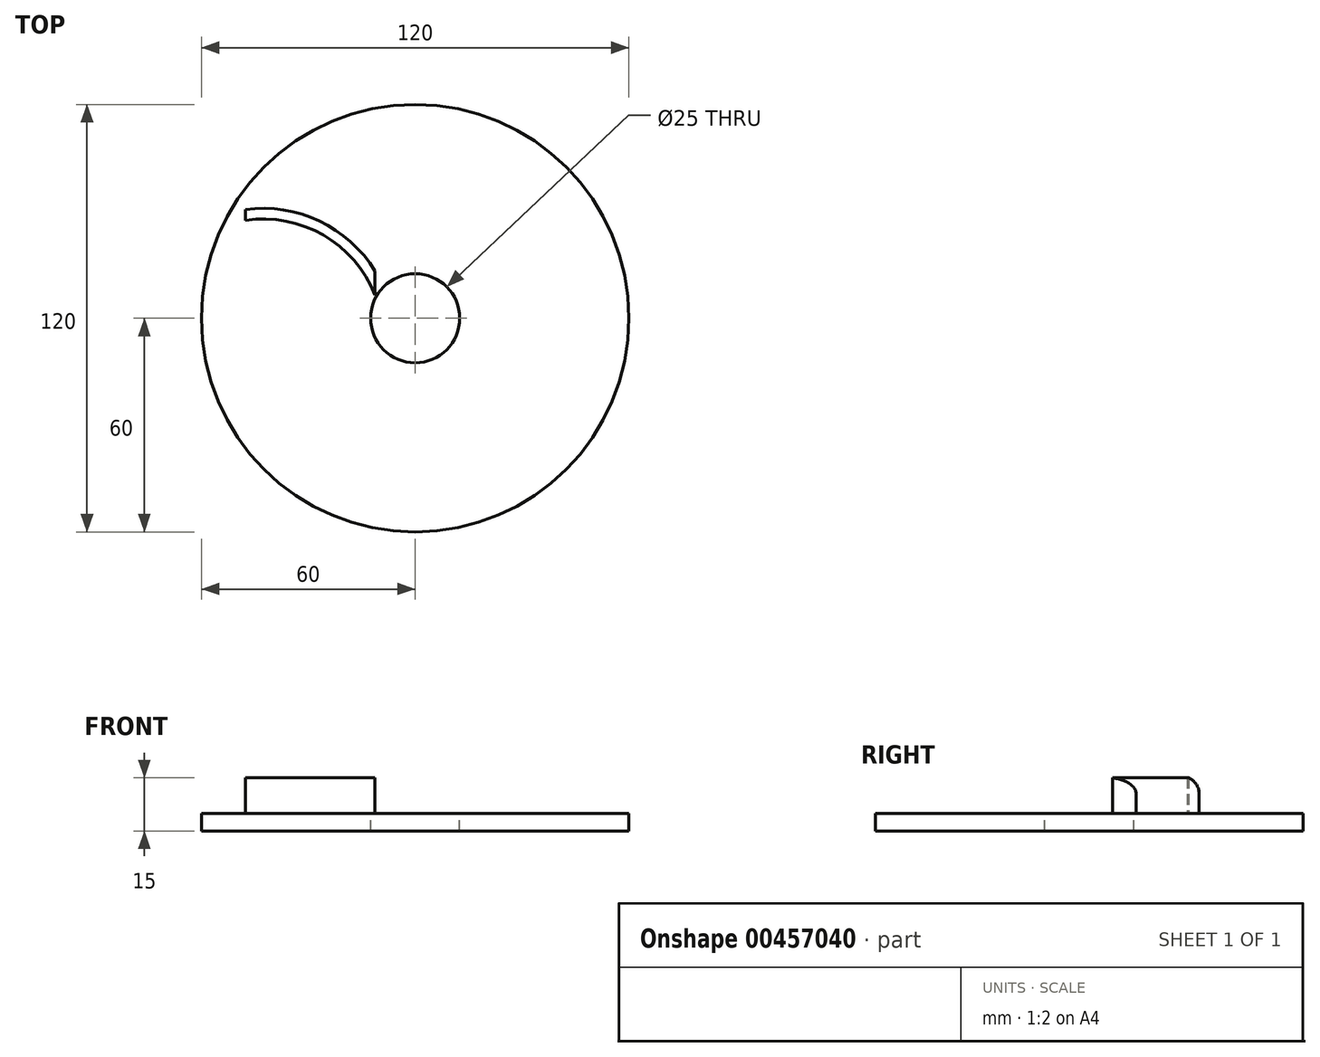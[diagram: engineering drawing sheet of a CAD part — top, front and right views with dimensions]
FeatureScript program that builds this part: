
annotation { "Feature Type Name" : "Feature", "Feature Type Description" : "" }
export const myFeature = defineFeature(function(context is Context, id is Id, definition is map)
    precondition{}
    {
        {
            var Q0;
            Q0=qCreatedBy(makeId("Top.planeOp"),FACE);
            var sketch = newSketch(context, id + "F0", { "sketchPlane" : qUnion([Q0])});
            skCircle(sketch, "E0", {"center": v(0, 0) * mm, "radius": 60 * mm});
            skSolve(sketch);
        }
        {
            var Q0;
            Q0 = qSketchRegion(id + "F0", true);
            extrude(context, id + "F1", {"entities" : qUnion([Q0]), "depth" : 5 * mm});
        }
        {
            var Q0;
            Q0=makeQuery(id+"F1.opExtrude","CAP_FACE",FACE,{"disambiguationData":[OSD([sQuery(id+"F0.wireOp",EDGE,"E0")])],"isStart":false});
            var sketch = newSketch(context, id + "F2", { "sketchPlane" : qUnion([Q0])});
            skCircle(sketch, "E1", {"center": v(0, 0) * mm, "radius": 12.5 * mm});
            skSolve(sketch);
        }
        {
            var Q0;
            Q0=makeQuery(id+"F2.imprint","IMPRINT",FACE,{"disambiguationData":[TD([[makeQuery(id+"F2.imprint","IMPRINT",EDGE,{"derivedFrom":sQuery(id+"F2.wireOp",EDGE,"E1")}),1.0]])]});
            extrude(context, id + "F3", {"entities" : qUnion([Q0]), "operationType" : NewBodyOperationType.REMOVE, "oppositeDirection" : true, "depth" : 10 * mm});
        }
        {
            var Q0;
            Q0=makeQuery(id+"F1.opExtrude","CAP_FACE",FACE,{"disambiguationData":[OSD([sQuery(id+"F0.wireOp",EDGE,"E0")])],"isStart":false});
            var sketch = newSketch(context, id + "F4", { "sketchPlane" : qUnion([Q0])});
            skArc(sketch, "E2", {"start": v(-11.26, 6.5) * mm, "mid": v(-25.79, 23.34) * mm, "end": v(-47.63, 27.5) * mm});
            skArc(sketch, "E3.0", {"start": v(-11.26, 13.2) * mm, "mid": v(-26.86, 27.3) * mm, "end": v(-47.63, 30.53) * mm});
            skLineSegment(sketch, "E4", {"start": v(-47.63, 27.5) * mm, "end": v(-47.63, 30.53) * mm});
            skLineSegment(sketch, "E5", {"start": v(-11.26, 6.5) * mm, "end": v(-11.26, 13.2) * mm});
            skLineSegment(sketch, "E6", {"start": v(-59.28, 34.23) * mm, "end": v(0, 0) * mm, "construction": true});
            skLineSegment(sketch, "E7", {"start": v(0, 0) * mm, "end": v(-66.48, 0) * mm, "construction": true});
            skSolve(sketch);
        }
        {
            var Q0;
            Q0=makeQuery(id+"F4.imprint","IMPRINT",FACE,{"disambiguationData":[TD([[makeQuery(id+"F4.imprint","IMPRINT",EDGE,{"derivedFrom":sQuery(id+"F4.wireOp",EDGE,"E2")}),-1.0]])]});
            extrude(context, id + "F5", {"entities" : qUnion([Q0]), "operationType" : NewBodyOperationType.ADD, "depth" : 10 * mm});
        }
        {
            var Q0;
            Q0=makeQuery(id+"F5.opExtrude","CAP_EDGE",EDGE,{"disambiguationData":[OSD([sQuery(id+"F4.wireOp",EDGE,"E3.0")])],"isStart":false});
            fillet(context, id + "F6", {"entities" : qUnion([Q0]), "radius" : 5 * mm, "tangentPropagation" : true, "allowEdgeOverflow" : false});
        }
    });
